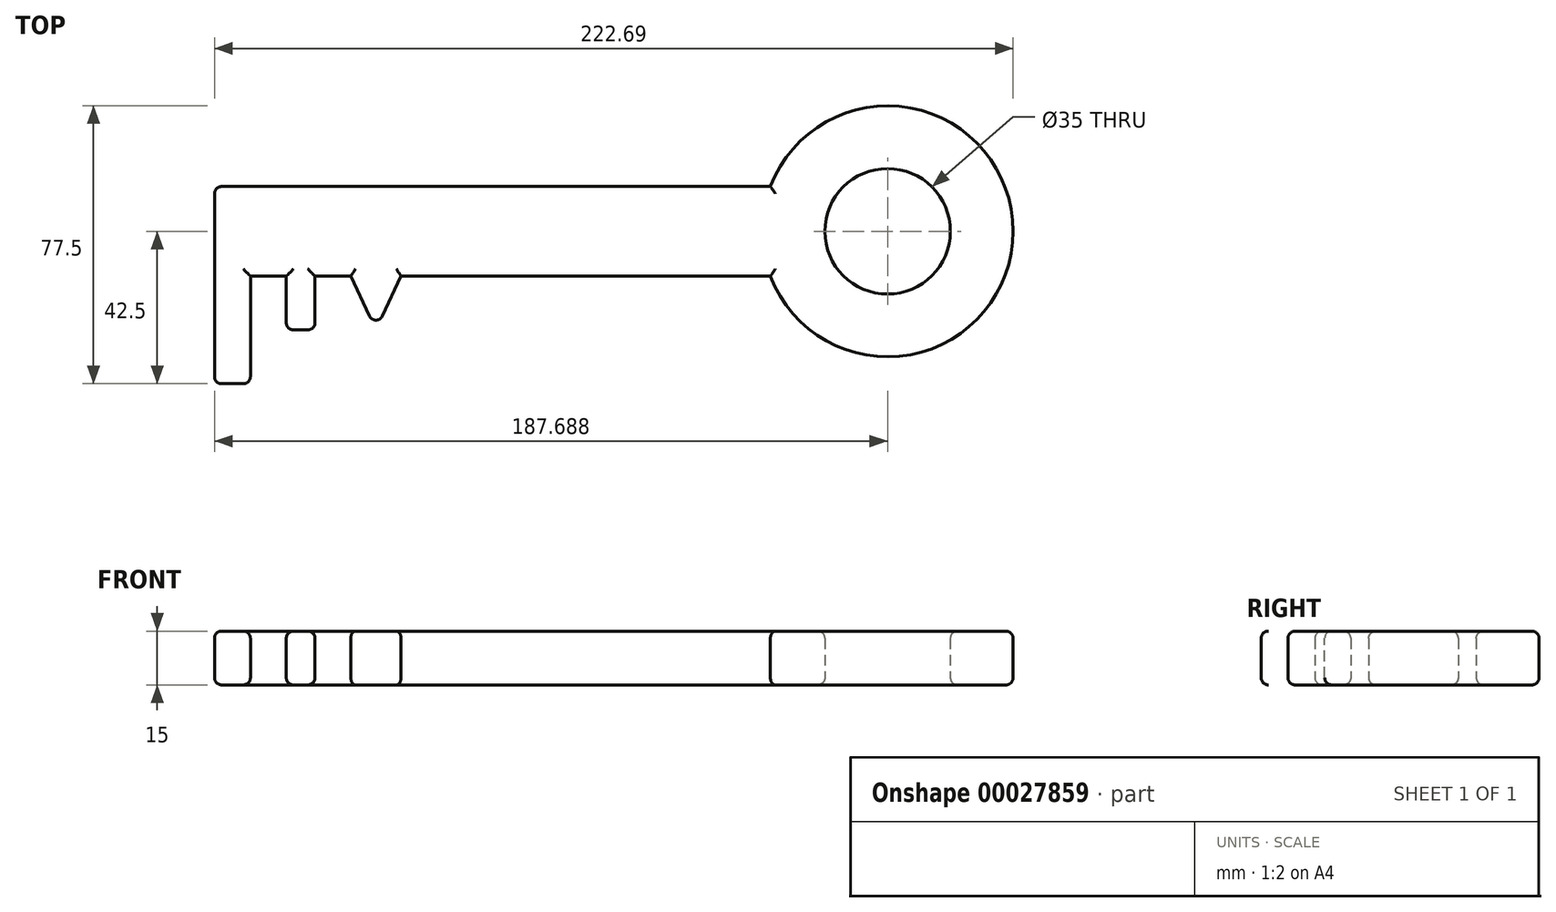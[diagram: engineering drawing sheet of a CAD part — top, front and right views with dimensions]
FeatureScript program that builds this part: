
annotation { "Feature Type Name" : "Feature", "Feature Type Description" : "" }
export const myFeature = defineFeature(function(context is Context, id is Id, definition is map)
    precondition{}
    {
        {
            var Q0;
            Q0=qCreatedBy(makeId("Top.planeOp"),FACE);
            var sketch = newSketch(context, id + "F0", { "sketchPlane" : qUnion([Q0])});
            skLineSegment(sketch, "E0.rect.bottom", {"start": v(-20.37, 40) * mm, "end": v(-175.37, 40) * mm});
            skLineSegment(sketch, "E0.rect.top", {"start": v(-20.37, 15) * mm, "end": v(-123.37, 15) * mm});
            skLineSegment(sketch, "E0.rect.right", {"start": v(-175.37, 40) * mm, "end": v(-175.37, 15) * mm});
            skPoint(sketch, "E0.rect.middle", {"position": v(-97.87, 27.5) * mm});
            skArc(sketch, "E1", {"start": v(-20.37, 15) * mm, "mid": v(47.32, 27.5) * mm, "end": v(-20.37, 40) * mm});
            skCircle(sketch, "E2", {"center": v(12.32, 27.5) * mm, "radius": 17.5 * mm});
            skLineSegment(sketch, "E3.top", {"start": v(-175.37, -15) * mm, "end": v(-165.37, -15) * mm});
            skLineSegment(sketch, "E3.left", {"start": v(-175.37, 15) * mm, "end": v(-175.37, -15) * mm});
            skLineSegment(sketch, "E3.right", {"start": v(-165.37, 15) * mm, "end": v(-165.37, -15) * mm});
            skLineSegment(sketch, "E4.top", {"start": v(-155.37, 0) * mm, "end": v(-147.37, 0) * mm});
            skLineSegment(sketch, "E4.left", {"start": v(-155.37, 15) * mm, "end": v(-155.37, 0) * mm});
            skLineSegment(sketch, "E4.right", {"start": v(-147.37, 15) * mm, "end": v(-147.37, 0) * mm});
            skLineSegment(sketch, "E5", {"start": v(-130.37, 0) * mm, "end": v(-137.37, 15) * mm});
            skLineSegment(sketch, "E6", {"start": v(-130.37, 0) * mm, "end": v(-123.37, 15) * mm});
            skLineSegment(sketch, "E7", {"start": v(-175.37, 27.5) * mm, "end": v(12.32, 27.5) * mm, "construction": true});
            skLineSegment(sketch, "E8.trimOffspring", {"start": v(-155.37, 15) * mm, "end": v(-165.37, 15) * mm});
            skLineSegment(sketch, "E9.trimOffspring", {"start": v(-137.37, 15) * mm, "end": v(-147.37, 15) * mm});
            skPoint(sketch, "E10.start.orphan", {"position": v(-130.37, 15) * mm});
            skSolve(sketch);
        }
        {
            var Q0;
            Q0=makeQuery(id+"F0.imprint","IMPRINT",FACE,{"disambiguationData":[TD([[makeQuery(id+"F0.imprint","IMPRINT",EDGE,{"derivedFrom":sQuery(id+"F0.wireOp",EDGE,"E0.rect.bottom")}),1.0]])]});
            extrude(context, id + "F1", {"entities" : qUnion([Q0]), "depth" : 15 * mm});
        }
        {
            var Q0;
            Q0=makeQuery(id+"F1.opExtrude","CAP_EDGE",EDGE,{"disambiguationData":[OSD([sQuery(id+"F0.wireOp",EDGE,"E0.rect.top")])],"isStart":false});
            var Q1;
            Q1=makeQuery(id+"F1.opExtrude","CAP_EDGE",EDGE,{"disambiguationData":[OSD([sQuery(id+"F0.wireOp",EDGE,"E6")])],"isStart":false});
            var Q2;
            Q2=makeQuery(id+"F1.opExtrude","CAP_EDGE",EDGE,{"disambiguationData":[OSD([sQuery(id+"F0.wireOp",EDGE,"E9.trimOffspring")])],"isStart":false});
            var Q3;
            Q3=makeQuery(id+"F1.opExtrude","CAP_EDGE",EDGE,{"disambiguationData":[OSD([sQuery(id+"F0.wireOp",EDGE,"E5")])],"isStart":false});
            var Q4;
            Q4=makeQuery(id+"F1.opExtrude","CAP_EDGE",EDGE,{"disambiguationData":[OSD([sQuery(id+"F0.wireOp",EDGE,"E4.right")])],"isStart":false});
            var Q5;
            Q5=makeQuery(id+"F1.opExtrude","CAP_EDGE",EDGE,{"disambiguationData":[OSD([sQuery(id+"F0.wireOp",EDGE,"E4.top")])],"isStart":false});
            var Q6;
            Q6=makeQuery(id+"F1.opExtrude","CAP_EDGE",EDGE,{"disambiguationData":[OSD([sQuery(id+"F0.wireOp",EDGE,"E4.left")])],"isStart":false});
            var Q7;
            Q7=makeQuery(id+"F1.opExtrude","CAP_EDGE",EDGE,{"disambiguationData":[OSD([sQuery(id+"F0.wireOp",EDGE,"E8.trimOffspring")])],"isStart":false});
            var Q8;
            Q8=makeQuery(id+"F1.opExtrude","CAP_EDGE",EDGE,{"disambiguationData":[OSD([sQuery(id+"F0.wireOp",EDGE,"E3.right")])],"isStart":false});
            var Q9;
            Q9=makeQuery(id+"F1.opExtrude","CAP_EDGE",EDGE,{"disambiguationData":[OSD([sQuery(id+"F0.wireOp",EDGE,"E3.top")])],"isStart":false});
            var Q10;
            Q10=makeQuery(id+"F1.opExtrude","CAP_EDGE",EDGE,{"disambiguationData":[OSD([sQuery(id+"F0.wireOp",EDGE,"E0.rect.right"),sQuery(id+"F0.wireOp",EDGE,"E3.left")])],"isStart":false});
            var Q11;
            Q11=makeQuery(id+"F1.opExtrude","CAP_EDGE",EDGE,{"disambiguationData":[OSD([sQuery(id+"F0.wireOp",EDGE,"E0.rect.bottom")])],"isStart":false});
            var Q12;
            Q12=makeQuery(id+"F1.opExtrude","CAP_EDGE",EDGE,{"disambiguationData":[OSD([sQuery(id+"F0.wireOp",EDGE,"E1")])],"isStart":false});
            var Q13;
            Q13=makeQuery(id+"F1.opExtrude","CAP_EDGE",EDGE,{"disambiguationData":[OSD([sQuery(id+"F0.wireOp",EDGE,"E2")])],"isStart":false});
            var Q14;
            Q14=makeQuery(id+"F1.opExtrude","CAP_EDGE",EDGE,{"disambiguationData":[OSD([sQuery(id+"F0.wireOp",EDGE,"E1")])],"isStart":true});
            var Q15;
            Q15=makeQuery(id+"F1.opExtrude","CAP_EDGE",EDGE,{"disambiguationData":[OSD([sQuery(id+"F0.wireOp",EDGE,"E2")])],"isStart":true});
            var Q16;
            Q16=makeQuery(id+"F1.opExtrude","CAP_EDGE",EDGE,{"disambiguationData":[OSD([sQuery(id+"F0.wireOp",EDGE,"E0.rect.top")])],"isStart":true});
            var Q17;
            Q17=makeQuery(id+"F1.opExtrude","CAP_EDGE",EDGE,{"disambiguationData":[OSD([sQuery(id+"F0.wireOp",EDGE,"E0.rect.bottom")])],"isStart":true});
            var Q18;
            Q18=makeQuery(id+"F1.opExtrude","CAP_EDGE",EDGE,{"disambiguationData":[OSD([sQuery(id+"F0.wireOp",EDGE,"E6")])],"isStart":true});
            var Q19;
            Q19=makeQuery(id+"F1.opExtrude","CAP_EDGE",EDGE,{"disambiguationData":[OSD([sQuery(id+"F0.wireOp",EDGE,"E5")])],"isStart":true});
            var Q20;
            Q20=makeQuery(id+"F1.opExtrude","CAP_EDGE",EDGE,{"disambiguationData":[OSD([sQuery(id+"F0.wireOp",EDGE,"E9.trimOffspring")])],"isStart":true});
            var Q21;
            Q21=makeQuery(id+"F1.opExtrude","CAP_EDGE",EDGE,{"disambiguationData":[OSD([sQuery(id+"F0.wireOp",EDGE,"E4.right")])],"isStart":true});
            var Q22;
            Q22=makeQuery(id+"F1.opExtrude","CAP_EDGE",EDGE,{"disambiguationData":[OSD([sQuery(id+"F0.wireOp",EDGE,"E4.top")])],"isStart":true});
            var Q23;
            Q23=makeQuery(id+"F1.opExtrude","CAP_EDGE",EDGE,{"disambiguationData":[OSD([sQuery(id+"F0.wireOp",EDGE,"E4.left")])],"isStart":true});
            var Q24;
            Q24=makeQuery(id+"F1.opExtrude","CAP_EDGE",EDGE,{"disambiguationData":[OSD([sQuery(id+"F0.wireOp",EDGE,"E8.trimOffspring")])],"isStart":true});
            var Q25;
            Q25=makeQuery(id+"F1.opExtrude","CAP_EDGE",EDGE,{"disambiguationData":[OSD([sQuery(id+"F0.wireOp",EDGE,"E3.right")])],"isStart":true});
            var Q26;
            Q26=makeQuery(id+"F1.opExtrude","CAP_EDGE",EDGE,{"disambiguationData":[OSD([sQuery(id+"F0.wireOp",EDGE,"E3.top")])],"isStart":true});
            var Q27;
            Q27=makeQuery(id+"F1.opExtrude","CAP_EDGE",EDGE,{"disambiguationData":[OSD([sQuery(id+"F0.wireOp",EDGE,"E0.rect.right"),sQuery(id+"F0.wireOp",EDGE,"E3.left")])],"isStart":true});
            var Q28;
            Q28=makeQuery(id+"F1.opExtrude","SWEPT_EDGE",EDGE,{"disambiguationData":[OSD([sQuery(id+"F0.wireOp",EDGE,"E5"),sQuery(id+"F0.wireOp",EDGE,"E6")])]});
            var Q29;
            Q29=makeQuery(id+"F1.opExtrude","SWEPT_EDGE",EDGE,{"disambiguationData":[OSD([sQuery(id+"F0.wireOp",EDGE,"E4.top"),sQuery(id+"F0.wireOp",EDGE,"E4.right")])]});
            var Q30;
            Q30=makeQuery(id+"F1.opExtrude","SWEPT_EDGE",EDGE,{"disambiguationData":[OSD([sQuery(id+"F0.wireOp",EDGE,"E4.top"),sQuery(id+"F0.wireOp",EDGE,"E4.left")])]});
            var Q31;
            Q31=makeQuery(id+"F1.opExtrude","SWEPT_EDGE",EDGE,{"disambiguationData":[OSD([sQuery(id+"F0.wireOp",EDGE,"E3.top"),sQuery(id+"F0.wireOp",EDGE,"E3.right")])]});
            var Q32;
            Q32=makeQuery(id+"F1.opExtrude","SWEPT_EDGE",EDGE,{"disambiguationData":[OSD([sQuery(id+"F0.wireOp",EDGE,"E3.top"),sQuery(id+"F0.wireOp",EDGE,"E3.left")])]});
            var Q33;
            Q33=makeQuery(id+"F1.opExtrude","SWEPT_EDGE",EDGE,{"disambiguationData":[OSD([sQuery(id+"F0.wireOp",EDGE,"E0.rect.bottom"),sQuery(id+"F0.wireOp",EDGE,"E0.rect.right")])]});
            fillet(context, id + "F2", {"entities" : qUnion([Q0, Q1, Q2, Q3, Q4, Q5, Q6, Q7, Q8, Q9, Q10, Q11, Q12, Q13, Q14, Q15, Q16, Q17, Q18, Q19, Q20, Q21, Q22, Q23, Q24, Q25, Q26, Q27, Q28, Q29, Q30, Q31, Q32, Q33]), "radius" : 2 * mm, "tangentPropagation" : true, "allowEdgeOverflow" : false});
        }
    });
